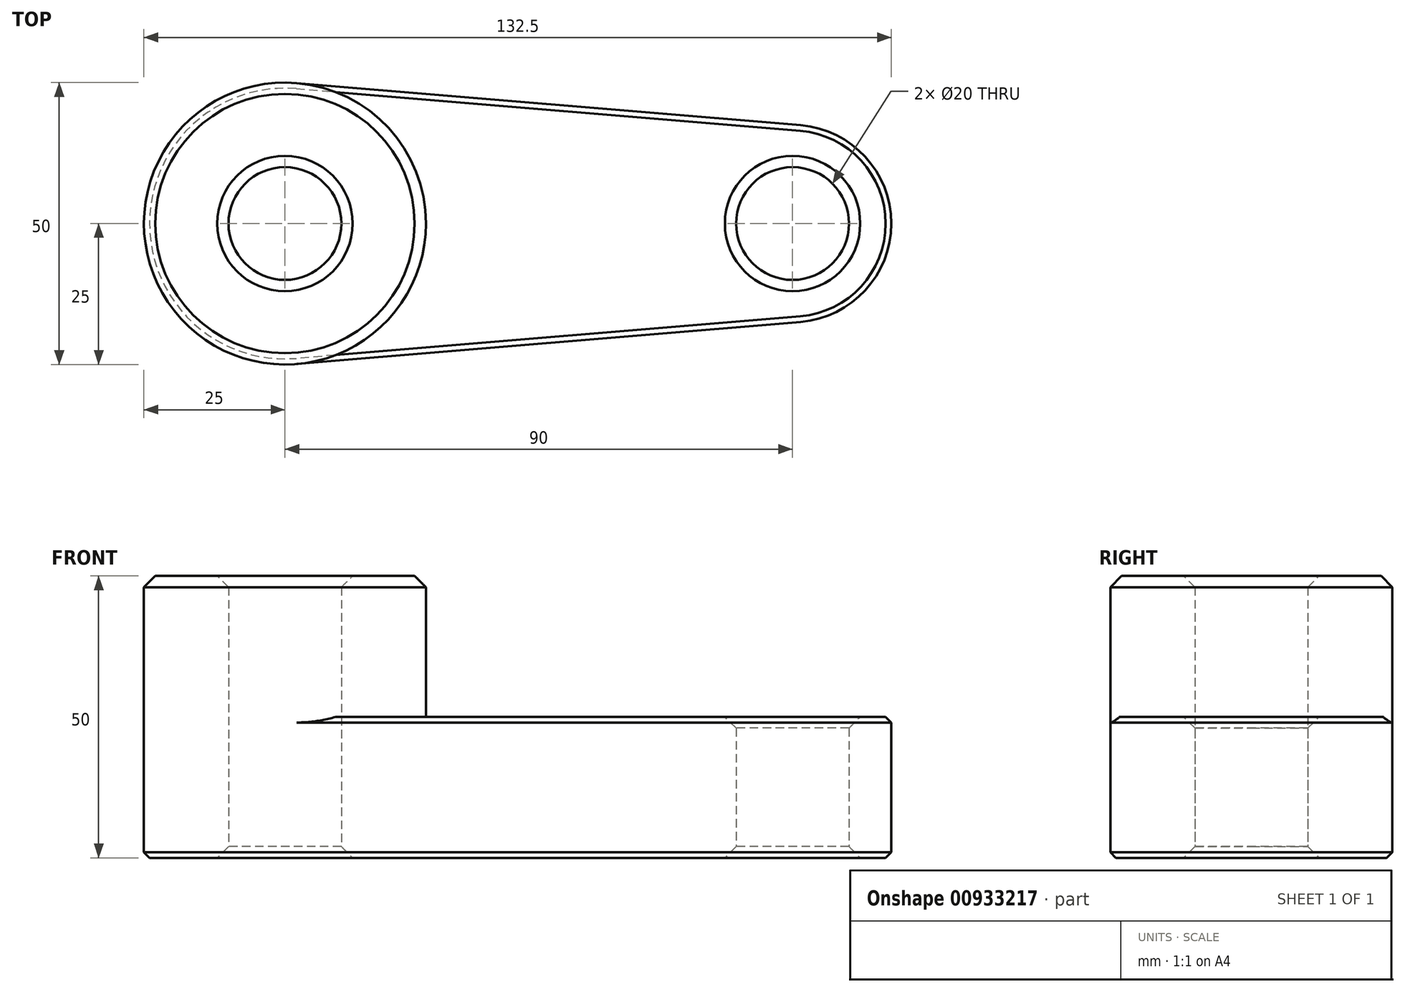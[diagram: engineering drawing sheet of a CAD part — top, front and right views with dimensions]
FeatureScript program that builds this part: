
annotation { "Feature Type Name" : "Feature", "Feature Type Description" : "" }
export const myFeature = defineFeature(function(context is Context, id is Id, definition is map)
    precondition{}
    {
        {
            var Q0;
            Q0=qCreatedBy(makeId("Top.planeOp"),FACE);
            var sketch = newSketch(context, id + "F0", { "sketchPlane" : qUnion([Q0])});
            skCircle(sketch, "E0", {"center": v(0, 0) * mm, "radius": 25 * mm});
            skCircle(sketch, "E1", {"center": v(90, 0) * mm, "radius": 17.5 * mm});
            skCircle(sketch, "E2", {"center": v(0, 0) * mm, "radius": 10 * mm});
            skCircle(sketch, "E3", {"center": v(90, 0) * mm, "radius": 10 * mm});
            skLineSegment(sketch, "E4", {"start": v(2.08, 24.91) * mm, "end": v(91.46, 17.44) * mm});
            skLineSegment(sketch, "E5", {"start": v(2.08, -24.91) * mm, "end": v(91.46, -17.44) * mm});
            skSolve(sketch);
        }
        {
            var Q0;
            Q0 = qSketchRegion(id + "F0", true);
            extrude(context, id + "F1", {"entities" : qUnion([Q0]), "depth" : 25 * mm, "offsetDistance" : 25 * mm});
        }
        {
            var Q0;
            Q0=makeQuery(id+"F0.imprint","IMPRINT",FACE,{"disambiguationData":[TD([[makeQuery(id+"F0.imprint","IMPRINT",EDGE,{"derivedFrom":sQuery(id+"F0.wireOp",EDGE,"E2")}),-1.0]])]});
            extrude(context, id + "F2", {"entities" : qUnion([Q0]), "operationType" : NewBodyOperationType.ADD, "depth" : 50 * mm, "offsetDistance" : 25 * mm});
        }
        {
            var Q0;
            Q0=makeQuery(id+"F2.opExtrude","CAP_EDGE",EDGE,{"disambiguationData":[OSD([sQuery(id+"F0.wireOp",EDGE,"E0")])],"isStart":false});
            var Q1;
            Q1=makeQuery(id+"F2.opExtrude","CAP_EDGE",EDGE,{"disambiguationData":[OSD([sQuery(id+"F0.wireOp",EDGE,"E2")])],"isStart":false});
            var Q2;
            Q2=makeQuery(id+"F1.opExtrude","CAP_EDGE",EDGE,{"disambiguationData":[OSD([sQuery(id+"F0.wireOp",EDGE,"E3")])],"isStart":false});
            var Q3;
            Q3=makeQuery(id+"F1.opExtrude","SWEPT_FACE",FACE,{"disambiguationData":[OSD([sQuery(id+"F0.wireOp",EDGE,"E3")])]});
            var Q4;
            Q4=makeQuery(id+"F1.opExtrude","CAP_EDGE",EDGE,{"disambiguationData":[OSD([sQuery(id+"F0.wireOp",EDGE,"E2")])],"isStart":true});
            chamfer(context, id + "F3", {"entities" : qUnion([Q0, Q1, Q2, Q3, Q4]), "width" : 2 * mm, "tangentPropagation" : true});
        }
        {
            var Q0;
            Q0=makeQuery(id+"F1.opExtrude","CAP_EDGE",EDGE,{"disambiguationData":[OSD([sQuery(id+"F0.wireOp",EDGE,"E5")])],"isStart":false});
            chamfer(context, id + "F4", {"entities" : qUnion([Q0]), "width" : 1 * mm, "tangentPropagation" : true});
        }
        {
            var Q0;
            Q0=makeQuery(id+"F1.opExtrude","CAP_EDGE",EDGE,{"disambiguationData":[OSD([sQuery(id+"F0.wireOp",EDGE,"E5")])],"isStart":true});
            chamfer(context, id + "F5", {"entities" : qUnion([Q0]), "width" : 1 * mm, "tangentPropagation" : true});
        }
    });
